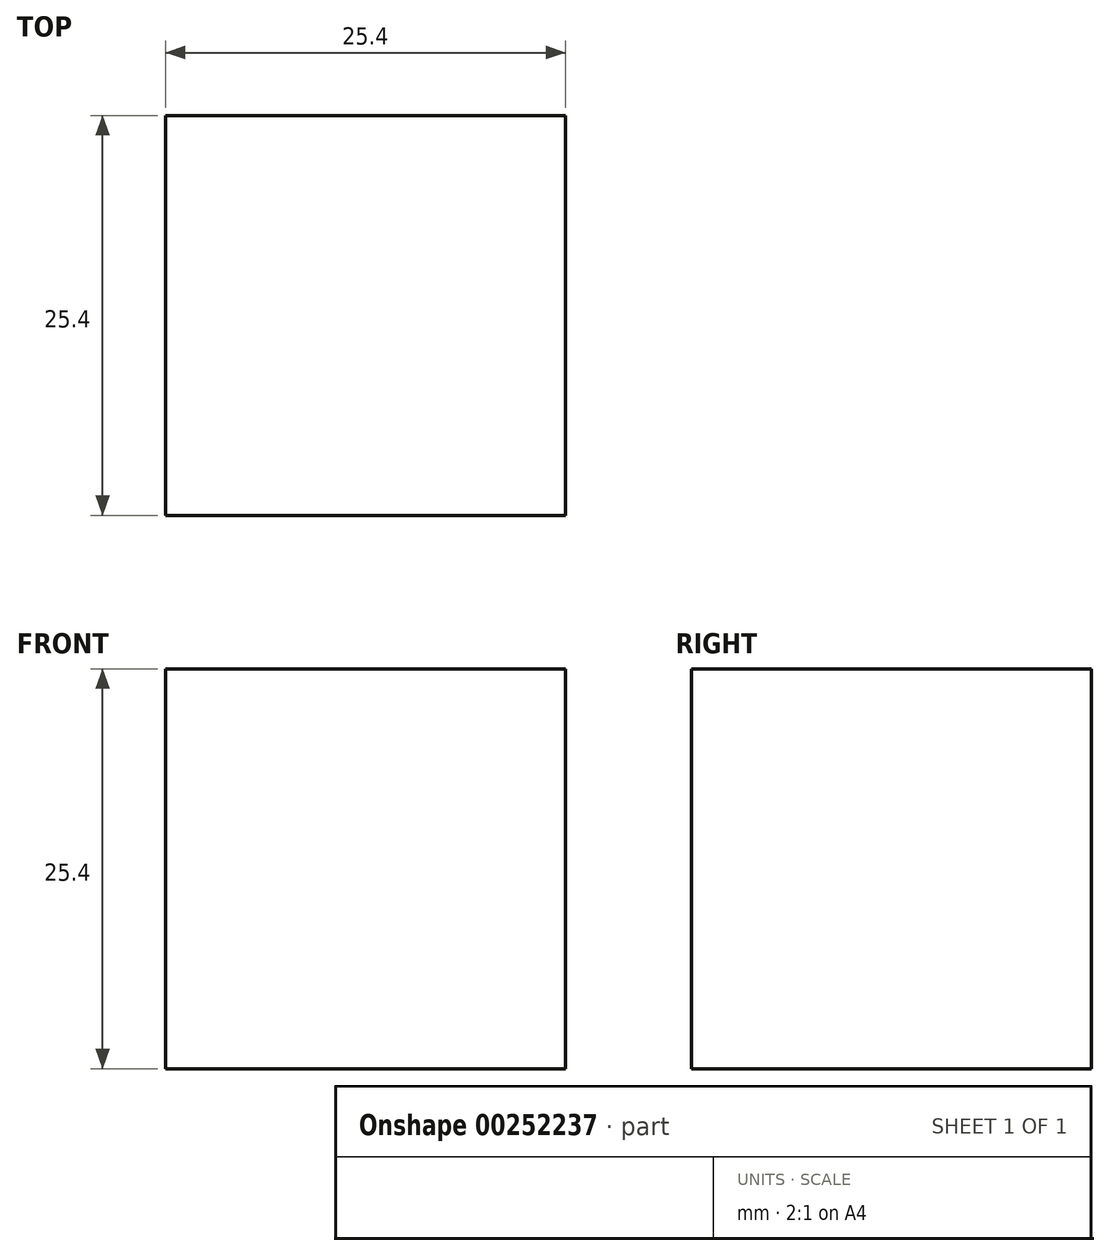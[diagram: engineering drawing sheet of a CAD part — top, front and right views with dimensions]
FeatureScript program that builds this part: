
annotation { "Feature Type Name" : "Feature", "Feature Type Description" : "" }
export const myFeature = defineFeature(function(context is Context, id is Id, definition is map)
    precondition{}
    {
        {
            var Q0;
            Q0=qCreatedBy(makeId("Right.planeOp"),FACE);
            var sketch = newSketch(context, id + "F0", { "sketchPlane" : qUnion([Q0])});
            skLineSegment(sketch, "E0.bottom", {"start": v(0, 0) * mm, "end": v(25.4, 0) * mm});
            skLineSegment(sketch, "E0.top", {"start": v(0, 25.4) * mm, "end": v(25.4, 25.4) * mm});
            skLineSegment(sketch, "E0.left", {"start": v(0, 0) * mm, "end": v(0, 25.4) * mm});
            skLineSegment(sketch, "E0.right", {"start": v(25.4, 0) * mm, "end": v(25.4, 25.4) * mm});
            skSolve(sketch);
        }
        {
            var Q0;
            Q0=makeQuery(id+"F0.imprint","IMPRINT",FACE,{"disambiguationData":[TD([[makeQuery(id+"F0.imprint","IMPRINT",EDGE,{"derivedFrom":sQuery(id+"F0.wireOp",EDGE,"E0.bottom")}),1.0]])]});
            extrude(context, id + "F1", {"entities" : qUnion([Q0]), "depth" : 25.4 * mm});
        }
    });
